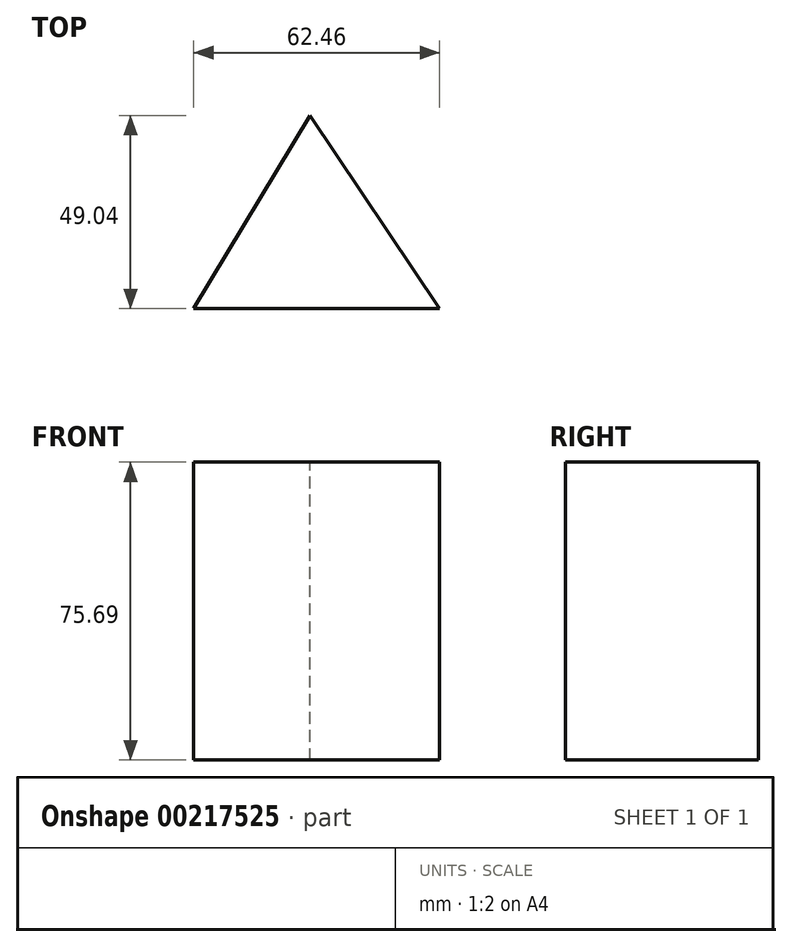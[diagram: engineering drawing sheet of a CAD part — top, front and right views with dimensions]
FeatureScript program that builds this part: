
annotation { "Feature Type Name" : "Feature", "Feature Type Description" : "" }
export const myFeature = defineFeature(function(context is Context, id is Id, definition is map)
    precondition{}
    {
        {
            var Q0;
            Q0=qCreatedBy(makeId("Top.planeOp"),FACE);
            var sketch = newSketch(context, id + "F0", { "sketchPlane" : qUnion([Q0])});
            skLineSegment(sketch, "E0", {"start": v(0, 0) * mm, "end": v(62.46, 0) * mm});
            skLineSegment(sketch, "E1", {"start": v(62.46, 0) * mm, "end": v(29.6, 49.04) * mm});
            skLineSegment(sketch, "E2", {"start": v(29.6, 49.04) * mm, "end": v(0, 0) * mm});
            skSolve(sketch);
        }
        {
            var Q0;
            Q0=makeQuery(id+"F0.imprint","IMPRINT",FACE,{"disambiguationData":[TD([[makeQuery(id+"F0.imprint","IMPRINT",EDGE,{"derivedFrom":sQuery(id+"F0.wireOp",EDGE,"E0")}),1.0]])]});
            extrude(context, id + "F1", {"entities" : qUnion([Q0]), "oppositeDirection" : true, "depth" : 75.7 * mm});
        }
    });
